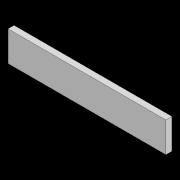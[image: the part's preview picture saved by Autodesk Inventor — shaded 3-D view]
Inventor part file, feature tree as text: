
AUTODESK INVENTOR PART (.ipt)
format: ipt  version: 2021 (Build 250183000, 183)  size: 76,288 bytes
history: native  units: in
note: dims shown in document units (in); Inventor stores cm internally (conversion verified against a paired STEP export)
features: extrude x1, sketch x1
ambient origin geometry x8: Origin, YZ Plane, XZ Plane, XY Plane, X Axis, Y Axis, Z Axis, Center Point
bodies: Solid1 (feature_tree)
feature tree (2):
  extrude  "Extrusion1"  Depth=0.7874in
  sketch  "Sketch1"  dims[d2=4.1339in d3=0.7874in d4=0.1575in d5=0.0in]
